# Revit family: ЗД РАШВОРК арт.202_201_221_215
name_source: partatom
category: Арматура трубопроводов
units: mm (PartAtom-declared; Revit-internal decimal feet)

## family parameters
Всегда вертикально = Да
На основе рабочей плоскости = Нет
Общий = Нет
При загрузке вырезать с полостями = Нет
Размер круглого соединителя = Использовать диаметр
Тип детали = Нормальный

## types (60) — shared parameters
ADSK_Единица измерения = шт
ADSK_Завод-изготовитель = ООО ТД "РАШВОРК"
URL = https://rwru.ru
Корпус = GG25
Угол = 60.00°
сдвиг = 4 мм
zero-valued in all types: Отметка по умолчанию

## per-type parameters (varying)
| type | ADSK_Масса | ADSK_Наименование краткое | B | DN | DNISO | HISO | dP | А | Е | Сторона | Управление |
| Затвор дисковый поворотный РАШВОРК 200-040-16, DN040, PN16, GG25 / GGG40 / EPDM, М/Ф, рукоятка, квадрат 9х9 | 2.7 | 200-040-16 | 140 мм | 40 мм | 65 мм | 10 мм | 82 мм | 70 мм | 33 мм | 30 мм | Управление : Рукоятка DN40_80 |
| Затвор дисковый поворотный РАШВОРК 200-050-16, DN050, PN16, GG25 / GGG40 / EPDM, М/Ф, рукоятка, квадрат 11х11 | 2.84 | 200-050-16 | 161 мм | 50 мм | 65 мм | 10 мм | 95 мм | 79 мм | 43 мм | 30 мм | Управление : Рукоятка DN40_80 |
| Затвор дисковый поворотный РАШВОРК 200-065-16, DN065, PN16, GG25 / GGG40 / EPDM, М/Ф, рукоятка, квадрат 11х11 | 3.29 | 200-065-16 | 160 мм | 65 мм | 70 мм | 10 мм | 108 мм | 93 мм | 46 мм | 35 мм | Управление : Рукоятка DN40_80 |
| Затвор дисковый поворотный РАШВОРК 200-080-16, DN080, PN16, GG25 / GGG40 / EPDM, М/Ф, рукоятка, квадрат 11х11 | 3.76 | 200-080-16 | 165 мм | 80 мм | 65 мм | 10 мм | 126 мм | 103 мм | 46 мм | 32 мм | Управление : Рукоятка DN40_80 |
| Затвор дисковый поворотный РАШВОРК 200-100-16, DN100, PN16, GG25 / GGG40 / EPDM, М/Ф, рукоятка, квадрат 11х11 | 5.5 | 200-100-16 | 185 мм | 100 мм | 90 мм | 12 мм | 155 мм | 120 мм | 52 мм | 43 мм | Управление : Рукоятка DN100_150 |
| Затвор дисковый поворотный РАШВОРК 200-125-16, DN125, PN16, GG25 / GGG40 / EPDM, М/Ф, рукоятка, квадрат 14х14 | 7.04 | 200-125-16 | 210 мм | 125 мм | 90 мм | 12 мм | 181 мм | 132 мм | 56 мм | 44 мм | Управление : Рукоятка DN100_150 |
| Затвор дисковый поворотный РАШВОРК 200-150-16, DN150, PN16, GG25 / GGG40 / EPDM, М/Ф, рукоятка, квадрат 14х14 | 8.03 | 200-150-16 | 210 мм | 150 мм | 90 мм | 12 мм | 202 мм | 158 мм | 56 мм | 44 мм | Управление : Рукоятка DN100_150 |
| Затвор дисковый поворотный РАШВОРК 200-200-16, DN200, PN16, GG25 / GGG40 / EPDM, М/Ф, рукоятка, квадрат 17х17 | 15.3 | 200-200-16 | 250 мм | 200 мм | 125 мм | 18 мм | 264 мм | 180 мм | 60 мм | 48 мм | Управление : Рукоятка DN200_250 |
| Затвор дисковый поворотный РАШВОРК 200-250-16, DN250, PN16, GG25 / GGG40 / EPDM, М/Ф, рукоятка, квадрат 22х22 | 22.5 | 200-250-16 | 295 мм | 250 мм | 125 мм | 18 мм | 317 мм | 215 мм | 68 мм | 58 мм | Управление : Рукоятка DN200_250 |
| Затвор дисковый поворотный РАШВОРК 200-300-16, DN300, PN16, GG25 / GGG40 / EPDM, М/Ф, редуктор, квадрат 22х22 | 30 | 200-300-16 | 320 мм | 300 мм | 125 мм | 18 мм | 372 мм | 251 мм | 78 мм | 58 мм | Управление : Редуктор 953 |
| Затвор дисковый поворотный РАШВОРК 200-350-16, DN350, PN16, GG25 / GGG40 / EPDM, М/Ф, редуктор, квадрат 22х22 | 64 | 200-350-16 | 346 мм | 350 мм | 150 мм | 18 мм | 425 мм | 262 мм | 78 мм | 60 мм | Управление : Редуктор 953 |
| Затвор дисковый поворотный РАШВОРК 200-400-16, DN400, PN16, GG25 / GGG40 / EPDM, М/Ф, редуктор, квадрат 27х27 | 74 | 200-400-16 | 375 мм | 400 мм | 175 мм | 20 мм | 482 мм | 300 мм | 102 мм | 80 мм | Управление : Редуктор 954 |
| Затвор дисковый поворотный РАШВОРК 200-450-16, DN450, PN16, GG25 / GGG40 / EPDM, М/Ф, редуктор, квадрат 27х27 | 123.3 | 200-450-16 | 400 мм | 450 мм | 175 мм | 20 мм | 536 мм | 333 мм | 114 мм | 90 мм | Управление : Редуктор 955_956 |
| Затвор дисковый поворотный РАШВОРК 200-500-16, DN500, PN16, GG25 / GGG40 / EPDM, М/Ф, редуктор, квадрат 32х32 | 149 | 200-500-16 | 432 мм | 500 мм | 175 мм | 20 мм | 590 мм | 366 мм | 127 мм | 80 мм | Управление : Редуктор 955_956 |
| Затвор дисковый поворотный РАШВОРК 200-600-16, DN600, PN16, GG25 / GGG40 / EPDM, М/Ф, редуктор, квадрат 36х36 | 266 | 200-600-16 | 562 мм | 600 мм | 210 мм | 30 мм | 694 мм | 447 мм | 154 мм | 115 мм | Управление : Редуктор 955_956 |
| Затвор дисковый поворотный РАШВОРК 201-040-16, DN040, PN16, GG25 / CF8 / EPDM, М/Ф, рукоятка, квадрат 9х9 | 2.7 | 201-040-16 | 140 мм | 40 мм | 65 мм | 10 мм | 82 мм | 70 мм | 33 мм | 30 мм | Управление : Рукоятка DN40_80 |
| Затвор дисковый поворотный РАШВОРК 201-050-16, DN050, PN16, GG25 / CF8 / EPDM, М/Ф, рукоятка, квадрат 11х11 | 2.84 | 201-050-16 | 161 мм | 50 мм | 65 мм | 10 мм | 95 мм | 79 мм | 43 мм | 30 мм | Управление : Рукоятка DN40_80 |
| Затвор дисковый поворотный РАШВОРК 201-065-16, DN065, PN16, GG25 / CF8 / EPDM, М/Ф, рукоятка, квадрат11х11 | 3.29 | 201-065-16 | 160 мм | 65 мм | 70 мм | 10 мм | 108 мм | 93 мм | 46 мм | 35 мм | Управление : Рукоятка DN40_80 |
| Затвор дисковый поворотный РАШВОРК 201-080-16, DN080, PN16, GG25 / CF8 / EPDM, М/Ф, рукоятка, квадрат 11х11 | 3.76 | 201-080-16 | 165 мм | 80 мм | 65 мм | 10 мм | 126 мм | 103 мм | 46 мм | 32 мм | Управление : Рукоятка DN40_80 |
| Затвор дисковый поворотный РАШВОРК 201-100-16, DN100, PN16, GG25 / CF8 / EPDM, М/Ф, рукоятка, квадрат 11х11 | 5.5 | 201-100-16 | 185 мм | 100 мм | 90 мм | 12 мм | 155 мм | 120 мм | 52 мм | 43 мм | Управление : Рукоятка DN100_150 |
| Затвор дисковый поворотный РАШВОРК 201-125-16, DN125, PN16, GG25 / CF8 / EPDM, М/Ф, рукоятка, квадрат 14х14 | 7.04 | 201-125-16 | 210 мм | 125 мм | 90 мм | 12 мм | 181 мм | 132 мм | 56 мм | 44 мм | Управление : Рукоятка DN100_150 |
| Затвор дисковый поворотный РАШВОРК 201-150-16, DN150, PN16, GG25 / CF8 / EPDM, М/Ф, рукоятка, квадрат 14х14 | 8.03 | 201-150-16 | 210 мм | 150 мм | 90 мм | 12 мм | 202 мм | 158 мм | 56 мм | 44 мм | Управление : Рукоятка DN100_150 |
| Затвор дисковый поворотный РАШВОРК 201-200-16, DN200, PN16, GG25 / CF8 / EPDM, М/Ф, рукоятка, квадрат 17х17 | 15.3 | 201-200-16 | 250 мм | 200 мм | 125 мм | 18 мм | 264 мм | 180 мм | 60 мм | 48 мм | Управление : Рукоятка DN200_250 |
| Затвор дисковый поворотный РАШВОРК 201-250-16, DN250, PN16, GG25 / CF8 / EPDM, М/Ф, рукоятка, квадрат 22х22 | 22.5 | 201-250-16 | 295 мм | 250 мм | 125 мм | 18 мм | 317 мм | 215 мм | 68 мм | 58 мм | Управление : Рукоятка DN200_250 |
| Затвор дисковый поворотный РАШВОРК 201-300-16, DN300, PN16, GG25 / CF8 / EPDM, М/Ф, редуктор, квадрат 22х22 | 30 | 201-300-16 | 320 мм | 300 мм | 125 мм | 18 мм | 372 мм | 251 мм | 78 мм | 58 мм | Управление : Редуктор 953 |
| Затвор дисковый поворотный РАШВОРК 201-350-16, DN350, PN16, GG25 / CF8 / EPDM, М/Ф, редуктор, квадрат 22х22 | 64 | 201-350-16 | 346 мм | 350 мм | 150 мм | 18 мм | 425 мм | 262 мм | 78 мм | 60 мм | Управление : Редуктор 953 |
| Затвор дисковый поворотный РАШВОРК 201-400-16, DN400, PN16, GG25 / CF8 / EPDM, М/Ф, редуктор, квадрат 27х27 | 74 | 201-400-16 | 375 мм | 400 мм | 175 мм | 20 мм | 482 мм | 300 мм | 102 мм | 80 мм | Управление : Редуктор 954 |
| Затвор дисковый поворотный РАШВОРК 201-450-16, DN450, PN16, GG25 / CF8 / EPDM, М/Ф, редуктор, квадрат 27х27 | 123.3 | 201-450-16 | 400 мм | 450 мм | 175 мм | 20 мм | 536 мм | 333 мм | 114 мм | 90 мм | Управление : Редуктор 955_956 |
| Затвор дисковый поворотный РАШВОРК 201-500-16, DN500, PN16, GG25 / CF8 / EPDM, М/Ф, редуктор, квадрат 32х32 | 149 | 201-500-16 | 432 мм | 500 мм | 175 мм | 20 мм | 590 мм | 366 мм | 127 мм | 80 мм | Управление : Редуктор 955_956 |
| Затвор дисковый поворотный РАШВОРК 201-600-16, DN600, PN16, GG25 / CF8 / EPDM, М/Ф, редуктор, квадрат 36х36 | 266 | 201-600-16 | 562 мм | 600 мм | 210 мм | 30 мм | 694 мм | 447 мм | 154 мм | 115 мм | Управление : Редуктор 955_956 |
| Затвор дисковый поворотный РАШВОРК 211-040-16, DN040, PN16, GG25 / CF8 / NBR, М/Ф, рукоятка, квадрат 9х9 | 2.7 | 211-040-16 | 140 мм | 40 мм | 65 мм | 10 мм | 82 мм | 70 мм | 33 мм | 30 мм | Управление : Рукоятка DN40_80 |
| Затвор дисковый поворотный РАШВОРК 211-050-16, DN050, PN16, GG25 / CF8 / NBR, М/Ф, рукоятка, квадрат 11х11 | 2.84 | 211-050-16 | 161 мм | 50 мм | 65 мм | 10 мм | 95 мм | 79 мм | 43 мм | 30 мм | Управление : Рукоятка DN40_80 |
| Затвор дисковый поворотный РАШВОРК 211-065-16, DN065, PN16, GG25 / CF8 / NBR, М/Ф, рукоятка, квадрат 11х11 | 3.29 | 211-065-16 | 160 мм | 65 мм | 70 мм | 10 мм | 108 мм | 93 мм | 46 мм | 35 мм | Управление : Рукоятка DN40_80 |
| Затвор дисковый поворотный РАШВОРК 211-080-16, DN080, PN16, GG25 / CF8 / NBR, М/Ф, рукоятка, квадрат 11х11 | 3.76 | 211-080-16 | 165 мм | 80 мм | 65 мм | 10 мм | 126 мм | 103 мм | 46 мм | 32 мм | Управление : Рукоятка DN40_80 |
| Затвор дисковый поворотный РАШВОРК 211-100-16, DN100, PN16, GG25 / CF8 / NBR, М/Ф, рукоятка, квадрат 11х11 | 5.5 | 211-100-16 | 185 мм | 100 мм | 90 мм | 12 мм | 155 мм | 120 мм | 52 мм | 43 мм | Управление : Рукоятка DN100_150 |
| Затвор дисковый поворотный РАШВОРК 211-125-16, DN125, PN16, GG25 / CF8 / NBR, М/Ф, рукоятка, квадрат 14х14 | 7.04 | 211-125-16 | 210 мм | 125 мм | 90 мм | 12 мм | 181 мм | 132 мм | 56 мм | 44 мм | Управление : Рукоятка DN100_150 |
| Затвор дисковый поворотный РАШВОРК 211-150-16, DN150, PN16, GG25 / CF8 / NBR, М/Ф, рукоятка, квадрат 14х14 | 8.03 | 211-150-16 | 210 мм | 150 мм | 90 мм | 12 мм | 202 мм | 158 мм | 56 мм | 44 мм | Управление : Рукоятка DN100_150 |
| Затвор дисковый поворотный РАШВОРК 211-200-16, DN200, PN16, GG25 / CF8 / NBR, М/Ф, рукоятка, квадрат 17х17 | 15.3 | 211-200-16 | 250 мм | 200 мм | 125 мм | 18 мм | 264 мм | 180 мм | 60 мм | 48 мм | Управление : Рукоятка DN200_250 |
| Затвор дисковый поворотный РАШВОРК 211-250-16, DN250, PN16, GG25 / CF8 / NBR, М/Ф, рукоятка, квадрат 22х22 | 22.5 | 211-250-16 | 295 мм | 250 мм | 125 мм | 18 мм | 317 мм | 215 мм | 68 мм | 58 мм | Управление : Рукоятка DN200_250 |
| Затвор дисковый поворотный РАШВОРК 211-300-16, DN300, PN16, GG25 / CF8 / NBR, М/Ф, редуктор, квадрат 22х22 | 30 | 211-300-16 | 320 мм | 300 мм | 125 мм | 18 мм | 372 мм | 251 мм | 78 мм | 58 мм | Управление : Редуктор 953 |
| Затвор дисковый поворотный РАШВОРК 211-350-16, DN350, PN16, GG25 / CF8 / NBR, М/Ф, редуктор, квадрат 22х22 | 64 | 211-350-16 | 346 мм | 350 мм | 150 мм | 18 мм | 425 мм | 262 мм | 78 мм | 60 мм | Управление : Редуктор 953 |
| Затвор дисковый поворотный РАШВОРК 211-400-16, DN400, PN16, GG25 / CF8 / NBR, М/Ф, редуктор, квадрат 27х27 | 74 | 211-400-16 | 375 мм | 400 мм | 175 мм | 20 мм | 482 мм | 300 мм | 102 мм | 80 мм | Управление : Редуктор 954 |
| Затвор дисковый поворотный РАШВОРК 211-450-16, DN450, PN16, GG25 / CF8 / NBR, М/Ф, редуктор, квадрат 27х27 | 123.3 | 211-450-16 | 400 мм | 450 мм | 175 мм | 20 мм | 536 мм | 333 мм | 114 мм | 90 мм | Управление : Редуктор 955_956 |
| Затвор дисковый поворотный РАШВОРК 211-500-16, DN500, PN16, GG25 / CF8 / NBR, М/Ф, редуктор, квадрат 32х32 | 149 | 211-500-16 | 432 мм | 500 мм | 175 мм | 20 мм | 590 мм | 366 мм | 127 мм | 80 мм | Управление : Редуктор 955_956 |
| Затвор дисковый поворотный РАШВОРК 211-600-16, DN600, PN16, GG25 / CF8 / NBR, М/Ф, редуктор, квадрат 36х36 | 266 | 211-600-16 | 562 мм | 600 мм | 210 мм | 30 мм | 694 мм | 447 мм | 154 мм | 115 мм | Управление : Редуктор 955_956 |
| Затвор дисковый поворотный РАШВОРК 215-040-16, DN040, PN16, GG25 / CF8 / VITON, М/Ф, рукоятка, квадрат 9х9 | 2.7 | 215-040-16 | 140 мм | 40 мм | 65 мм | 10 мм | 82 мм | 70 мм | 33 мм | 30 мм | Управление : Рукоятка DN40_80 |
| Затвор дисковый поворотный РАШВОРК 215-050-16, DN050, PN16, GG25 / CF8 / VITON, М/Ф, рукоятка, квадрат 11х11 | 2.84 | 215-050-16 | 161 мм | 50 мм | 65 мм | 10 мм | 95 мм | 79 мм | 43 мм | 30 мм | Управление : Рукоятка DN40_80 |
| Затвор дисковый поворотный РАШВОРК 215-065-16, DN065, PN16, GG25 / CF8 / VITON, М/Ф, рукоятка, квадрат 11х11 | 3.29 | 215-065-16 | 160 мм | 65 мм | 70 мм | 10 мм | 108 мм | 93 мм | 46 мм | 35 мм | Управление : Рукоятка DN40_80 |
| Затвор дисковый поворотный РАШВОРК 215-080-16, DN080, PN16, GG25 / CF8 / VITON, М/Ф, рукоятка, квадрат 11х11 | 3.76 | 215-080-16 | 165 мм | 80 мм | 65 мм | 10 мм | 126 мм | 103 мм | 46 мм | 32 мм | Управление : Рукоятка DN40_80 |
| Затвор дисковый поворотный РАШВОРК 215-100-16, DN100, PN16, GG25 / CF8 / VITON, М/Ф, рукоятка, квадрат 11х11 | 5.5 | 215-100-16 | 185 мм | 100 мм | 90 мм | 12 мм | 155 мм | 120 мм | 52 мм | 43 мм | Управление : Рукоятка DN100_150 |
| Затвор дисковый поворотный РАШВОРК 215-125-16, DN125, PN16, GG25 / CF8 / VITON, М/Ф, рукоятка, квадрат 14х14 | 7.04 | 215-125-16 | 210 мм | 125 мм | 90 мм | 12 мм | 181 мм | 132 мм | 56 мм | 44 мм | Управление : Рукоятка DN100_150 |
| Затвор дисковый поворотный РАШВОРК 215-150-16, DN150, PN16, GG25 / CF8 / VITON, М/Ф, рукоятка, квадрат 14х14 | 8.03 | 215-150-16 | 210 мм | 150 мм | 90 мм | 12 мм | 202 мм | 158 мм | 56 мм | 44 мм | Управление : Рукоятка DN100_150 |
| Затвор дисковый поворотный РАШВОРК 215-200-16, DN200, PN16, GG25 / CF8 / VITON, М/Ф, рукоятка, квадрат 17х17 | 15.3 | 215-200-16 | 250 мм | 200 мм | 125 мм | 18 мм | 264 мм | 180 мм | 60 мм | 48 мм | Управление : Рукоятка DN200_250 |
| Затвор дисковый поворотный РАШВОРК 215-250-16, DN250, PN16, GG25 / CF8 / VITON, М/Ф, рукоятка, квадрат 22х22 | 22.5 | 215-250-16 | 295 мм | 250 мм | 125 мм | 18 мм | 317 мм | 215 мм | 68 мм | 58 мм | Управление : Рукоятка DN200_250 |
| Затвор дисковый поворотный РАШВОРК 215-300-16, DN300, PN16, GG25 / CF8 / VITON, М/Ф, редуктор, квадрат 22х22 | 30 | 215-300-16 | 320 мм | 300 мм | 125 мм | 18 мм | 372 мм | 251 мм | 78 мм | 58 мм | Управление : Редуктор 953 |
| Затвор дисковый поворотный РАШВОРК 215-350-16, DN350, PN16, GG25 / CF8/ VITON, М/Ф, редуктор, квадрат 22х22 | 64 | 215-350-16 | 346 мм | 350 мм | 150 мм | 18 мм | 425 мм | 262 мм | 78 мм | 60 мм | Управление : Редуктор 953 |
| Затвор дисковый поворотный РАШВОРК 215-400-16, DN400, PN16, GG25 / CF8 / VITON, М/Ф, редуктор, квадрат 27х27 | 74 | 215-400-16 | 375 мм | 400 мм | 175 мм | 20 мм | 482 мм | 300 мм | 102 мм | 80 мм | Управление : Редуктор 954 |
| Затвор дисковый поворотный РАШВОРК 215-450-16, DN450, PN16, GG25 / CF8 / VITON, М/Ф, редуктор, квадрат 27х27 | 123.3 | 215-450-16 | 400 мм | 450 мм | 175 мм | 20 мм | 536 мм | 333 мм | 114 мм | 90 мм | Управление : Редуктор 955_956 |
| Затвор дисковый поворотный РАШВОРК 215-500-16, DN500, PN16, GG25 / CF8 / VITON, М/Ф, редуктор, квадрат 32х32 | 149 | 215-500-16 | 432 мм | 500 мм | 175 мм | 20 мм | 590 мм | 366 мм | 127 мм | 80 мм | Управление : Редуктор 955_956 |
| Затвор дисковый поворотный РАШВОРК 215-600-16, DN600, PN16, GG25 / CF8 / VITON, М/Ф, редуктор, квадрат 36х36 | 266 | 215-600-16 | 562 мм | 600 мм | 210 мм | 30 мм | 694 мм | 447 мм | 154 мм | 115 мм | Управление : Редуктор 955_956 |

note: column(s) folded — value = type name in every type: ADSK_Наименование

## geometry (parser evidence)
native form markers: Blend x4
no freeform markers — native parametric forms only
